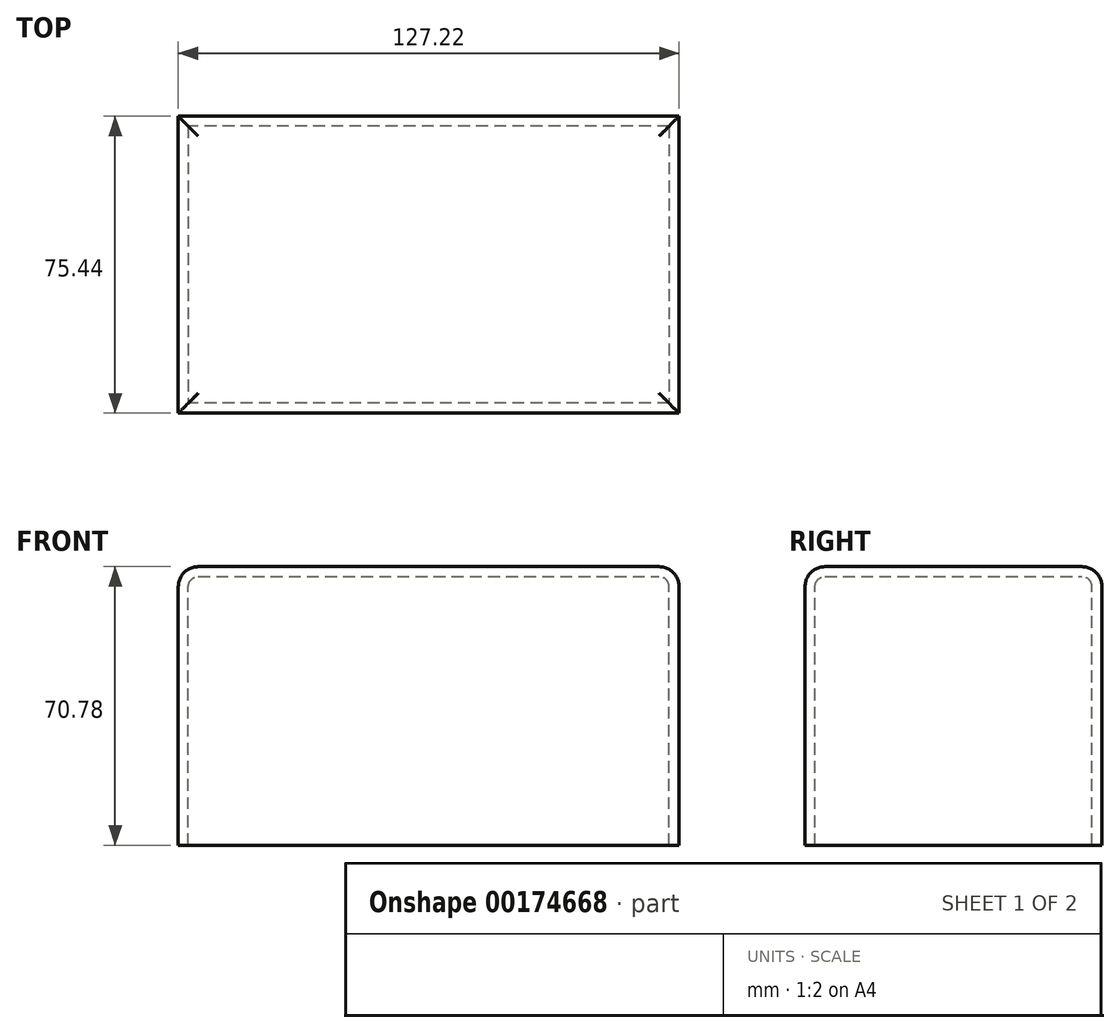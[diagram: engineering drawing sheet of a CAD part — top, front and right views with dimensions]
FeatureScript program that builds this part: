
annotation { "Feature Type Name" : "Feature", "Feature Type Description" : "" }
export const myFeature = defineFeature(function(context is Context, id is Id, definition is map)
    precondition{}
    {
        {
            var Q0;
            Q0=qCreatedBy(makeId("Front.planeOp"),FACE);
            var sketch = newSketch(context, id + "F0", { "sketchPlane" : qUnion([Q0])});
            skLineSegment(sketch, "E0.bottom", {"start": v(0, 0) * mm, "end": v(-127.22, 0) * mm});
            skLineSegment(sketch, "E0.top", {"start": v(0, 70.78) * mm, "end": v(-127.22, 70.78) * mm});
            skLineSegment(sketch, "E0.left", {"start": v(0, 0) * mm, "end": v(0, 70.78) * mm});
            skLineSegment(sketch, "E0.right", {"start": v(-127.22, 0) * mm, "end": v(-127.22, 70.78) * mm});
            skSolve(sketch);
        }
        {
            var Q0;
            Q0=makeQuery(id+"F0.imprint","IMPRINT",FACE,{"disambiguationData":[TD([[makeQuery(id+"F0.imprint","IMPRINT",EDGE,{"derivedFrom":sQuery(id+"F0.wireOp",EDGE,"E0.bottom")}),-1.0]])]});
            extrude(context, id + "F1", {"entities" : qUnion([Q0]), "oppositeDirection" : true, "depth" : 75.44 * mm});
        }
        {
            var Q0;
            Q0=makeQuery(id+"F1.opExtrude","SWEPT_EDGE",EDGE,{"disambiguationData":[OSD([sQuery(id+"F0.wireOp",EDGE,"E0.top"),sQuery(id+"F0.wireOp",EDGE,"E0.left")])]});
            var Q1;
            Q1=makeQuery(id+"F1.opExtrude","SWEPT_FACE",FACE,{"disambiguationData":[OSD([sQuery(id+"F0.wireOp",EDGE,"E0.top")])]});
            fillet(context, id + "F2", {"entities" : qUnion([Q0, Q1]), "radius" : 5.08 * mm, "tangentPropagation" : true, "allowEdgeOverflow" : false});
        }
        {
            var Q0;
            Q0=makeQuery(id+"F1.opExtrude","SWEPT_FACE",FACE,{"disambiguationData":[OSD([sQuery(id+"F0.wireOp",EDGE,"E0.bottom")])]});
            shell(context, id + "F3", {"entities" : qUnion([Q0]), "thickness" : 2.54 * mm});
        }
    });
